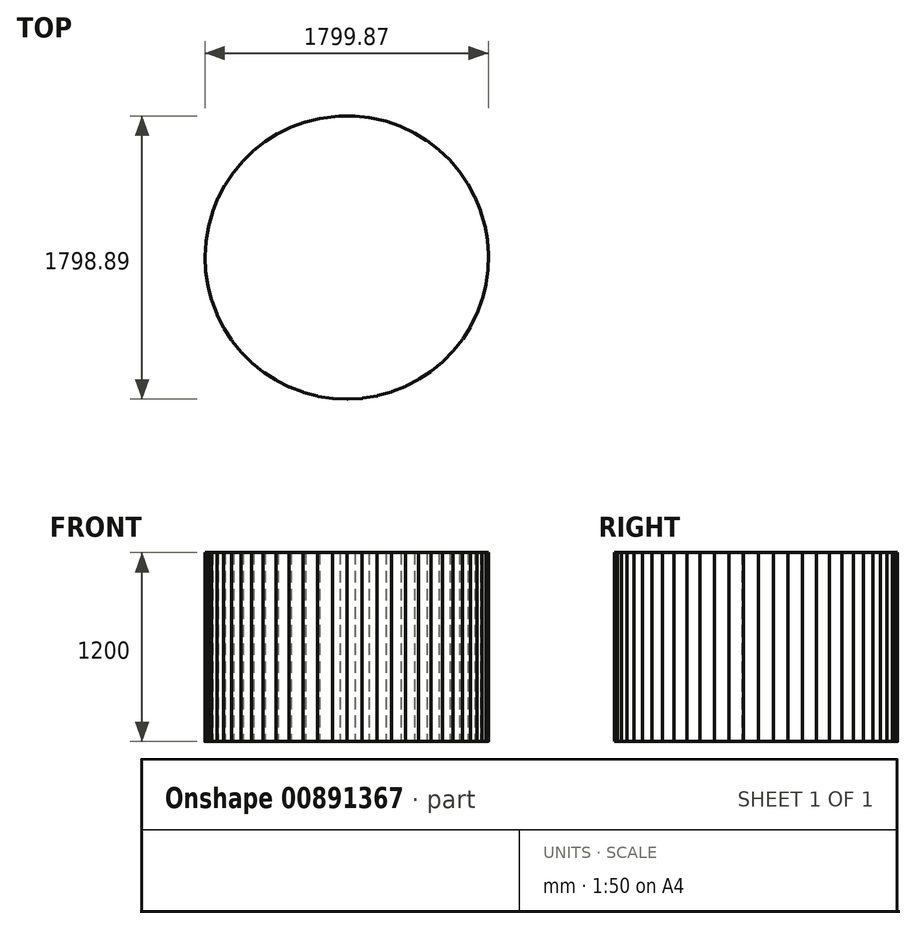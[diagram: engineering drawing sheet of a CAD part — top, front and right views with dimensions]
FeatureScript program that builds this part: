
annotation { "Feature Type Name" : "Feature", "Feature Type Description" : "" }
export const myFeature = defineFeature(function(context is Context, id is Id, definition is map)
    precondition{}
    {
        {
            var Q0;
            Q0=qCreatedBy(makeId("Top.planeOp"),FACE);
            var sketch = newSketch(context, id + "F0", { "sketchPlane" : qUnion([Q0])});
            skLineSegment(sketch, "E0.bottom", {"start": v(-48.1, 898.71) * mm, "end": v(46.9, 898.71) * mm});
            skLineSegment(sketch, "E0.top", {"start": v(-48.1, 853.71) * mm, "end": v(46.9, 853.71) * mm});
            skArc(sketch, "E1", {"start": v(46.9, 853.71) * mm, "mid": v(69.4, 876.21) * mm, "end": v(46.9, 898.71) * mm});
            skLineSegment(sketch, "E2", {"start": v(46.9, 898.71) * mm, "end": v(141.37, 888.83) * mm});
            skLineSegment(sketch, "E3.0", {"start": v(42.2, 853.96) * mm, "end": v(136.69, 844.07) * mm});
            skArc(sketch, "E4", {"start": v(141.37, 888.83) * mm, "mid": v(161.4, 864.1) * mm, "end": v(136.69, 844.07) * mm});
            skLineSegment(sketch, "E5", {"start": v(141.37, 888.83) * mm, "end": v(249.54, 864.71) * mm});
            skLineSegment(sketch, "E6.0", {"start": v(147.03, 841.46) * mm, "end": v(239.75, 820.8) * mm});
            skArc(sketch, "E7", {"start": v(249.54, 864.71) * mm, "mid": v(266.6, 837.86) * mm, "end": v(239.75, 820.8) * mm});
            skLineSegment(sketch, "E8", {"start": v(249.54, 864.71) * mm, "end": v(339.3, 833.6) * mm});
            skLineSegment(sketch, "E9", {"start": v(339.3, 833.6) * mm, "end": v(425.28, 793.18) * mm});
            skLineSegment(sketch, "E10", {"start": v(425.28, 793.18) * mm, "end": v(506.52, 743.94) * mm});
            skLineSegment(sketch, "E11", {"start": v(506.52, 743.94) * mm, "end": v(582.11, 686.4) * mm});
            skLineSegment(sketch, "E12", {"start": v(582.11, 686.4) * mm, "end": v(651.22, 621.22) * mm});
            skLineSegment(sketch, "E13", {"start": v(651.22, 621.22) * mm, "end": v(713.08, 549.11) * mm});
            skLineSegment(sketch, "E14", {"start": v(713.08, 549.11) * mm, "end": v(766.98, 470.89) * mm});
            skLineSegment(sketch, "E15", {"start": v(766.98, 470.89) * mm, "end": v(812.59, 386.91) * mm});
            skLineSegment(sketch, "E16", {"start": v(812.59, 386.91) * mm, "end": v(848.85, 299.1) * mm});
            skLineSegment(sketch, "E17", {"start": v(848.85, 299.1) * mm, "end": v(875.64, 207.96) * mm});
            skLineSegment(sketch, "E18", {"start": v(875.64, 207.96) * mm, "end": v(892.69, 114.5) * mm});
            skLineSegment(sketch, "E19", {"start": v(892.69, 114.5) * mm, "end": v(899.78, 19.77) * mm});
            skLineSegment(sketch, "E20", {"start": v(899.78, 19.77) * mm, "end": v(896.85, -75.19) * mm});
            skLineSegment(sketch, "E21", {"start": v(896.85, -75.19) * mm, "end": v(883.93, -169.3) * mm});
            skLineSegment(sketch, "E22.0", {"start": v(234.8, 822.2) * mm, "end": v(324.56, 791.07) * mm});
            skLineSegment(sketch, "E23.0", {"start": v(320.16, 792.87) * mm, "end": v(406.14, 752.46) * mm});
            skLineSegment(sketch, "E24.0", {"start": v(401.95, 754.7) * mm, "end": v(483.2, 705.45) * mm});
            skLineSegment(sketch, "E25.0", {"start": v(479.26, 708.13) * mm, "end": v(554.86, 650.6) * mm});
            skLineSegment(sketch, "E26.0", {"start": v(551.24, 653.66) * mm, "end": v(620.35, 588.48) * mm});
            skLineSegment(sketch, "E27.0", {"start": v(617.07, 591.92) * mm, "end": v(678.92, 519.81) * mm});
            skLineSegment(sketch, "E28.0", {"start": v(676.02, 523.58) * mm, "end": v(729.93, 445.35) * mm});
            skLineSegment(sketch, "E29.0", {"start": v(727.44, 449.41) * mm, "end": v(773.04, 365.44) * mm});
            skLineSegment(sketch, "E30.0", {"start": v(771, 369.74) * mm, "end": v(807.25, 281.93) * mm});
            skLineSegment(sketch, "E31.0", {"start": v(805.67, 286.4) * mm, "end": v(832.47, 195.27) * mm});
            skLineSegment(sketch, "E32.0", {"start": v(831.37, 199.89) * mm, "end": v(848.42, 106.43) * mm});
            skLineSegment(sketch, "E33.0", {"start": v(847.81, 111.14) * mm, "end": v(854.9, 16.4) * mm});
            skLineSegment(sketch, "E34.0", {"start": v(854.8, 21.15) * mm, "end": v(851.88, -73.8) * mm});
            skLineSegment(sketch, "E35.0", {"start": v(852.27, -69.07) * mm, "end": v(839.35, -163.18) * mm});
            skArc(sketch, "E36", {"start": v(339.3, 833.6) * mm, "mid": v(353.19, 804.96) * mm, "end": v(324.56, 791.07) * mm});
            skArc(sketch, "E37", {"start": v(425.28, 793.18) * mm, "mid": v(436.07, 763.25) * mm, "end": v(406.14, 752.46) * mm});
            skArc(sketch, "E38", {"start": v(506.52, 743.94) * mm, "mid": v(514.1, 713.03) * mm, "end": v(483.2, 705.45) * mm});
            skArc(sketch, "E39", {"start": v(582.11, 686.4) * mm, "mid": v(586.4, 654.87) * mm, "end": v(554.86, 650.6) * mm});
            skArc(sketch, "E40", {"start": v(651.22, 621.22) * mm, "mid": v(652.15, 589.4) * mm, "end": v(620.35, 588.48) * mm});
            skArc(sketch, "E41", {"start": v(713.08, 549.11) * mm, "mid": v(710.65, 517.38) * mm, "end": v(678.92, 519.81) * mm});
            skArc(sketch, "E42", {"start": v(766.98, 470.89) * mm, "mid": v(761.23, 439.6) * mm, "end": v(729.93, 445.35) * mm});
            skArc(sketch, "E43", {"start": v(812.59, 386.91) * mm, "mid": v(803.55, 356.4) * mm, "end": v(773.04, 365.44) * mm});
            skArc(sketch, "E44", {"start": v(848.85, 299.1) * mm, "mid": v(836.64, 269.72) * mm, "end": v(807.25, 281.93) * mm});
            skArc(sketch, "E45", {"start": v(875.64, 207.96) * mm, "mid": v(860.4, 180.03) * mm, "end": v(832.47, 195.27) * mm});
            skArc(sketch, "E46", {"start": v(892.69, 114.5) * mm, "mid": v(874.59, 88.33) * mm, "end": v(848.42, 106.43) * mm});
            skArc(sketch, "E47", {"start": v(899.78, 19.77) * mm, "mid": v(879.03, -4.35) * mm, "end": v(854.9, 16.4) * mm});
            skArc(sketch, "E48", {"start": v(896.85, -75.19) * mm, "mid": v(873.67, -96.98) * mm, "end": v(851.88, -73.8) * mm});
            skArc(sketch, "E49", {"start": v(839.35, -163.18) * mm, "mid": v(858.58, -188.54) * mm, "end": v(883.93, -169.3) * mm});
            skLineSegment(sketch, "E50", {"start": v(883.93, -169.3) * mm, "end": v(861.16, -261.54) * mm});
            skLineSegment(sketch, "E51", {"start": v(861.16, -261.54) * mm, "end": v(828.8, -350.85) * mm});
            skLineSegment(sketch, "E52", {"start": v(828.8, -350.85) * mm, "end": v(787.2, -436.26) * mm});
            skLineSegment(sketch, "E53", {"start": v(787.2, -436.26) * mm, "end": v(736.82, -516.8) * mm});
            skLineSegment(sketch, "E54", {"start": v(736.82, -516.8) * mm, "end": v(678.24, -591.6) * mm});
            skLineSegment(sketch, "E55", {"start": v(678.24, -591.6) * mm, "end": v(612.1, -659.8) * mm});
            skLineSegment(sketch, "E56", {"start": v(612.1, -659.8) * mm, "end": v(539.15, -720.64) * mm});
            skLineSegment(sketch, "E57", {"start": v(539.15, -720.64) * mm, "end": v(460.18, -773.45) * mm});
            skLineSegment(sketch, "E58", {"start": v(460.18, -773.45) * mm, "end": v(376.1, -817.65) * mm});
            skLineSegment(sketch, "E59", {"start": v(376.1, -817.65) * mm, "end": v(287.8, -852.74) * mm});
            skLineSegment(sketch, "E60", {"start": v(287.8, -852.74) * mm, "end": v(196.32, -878.33) * mm});
            skLineSegment(sketch, "E61", {"start": v(196.32, -878.33) * mm, "end": v(102.64, -894.13) * mm});
            skLineSegment(sketch, "E62", {"start": v(102.64, -894.13) * mm, "end": v(7.82, -899.97) * mm});
            skLineSegment(sketch, "E63", {"start": v(7.82, -899.97) * mm, "end": v(-87.09, -895.78) * mm});
            skLineSegment(sketch, "E64", {"start": v(-87.09, -895.78) * mm, "end": v(-181.02, -881.6) * mm});
            skLineSegment(sketch, "E65", {"start": v(-181.02, -881.6) * mm, "end": v(-272.94, -857.61) * mm});
            skLineSegment(sketch, "E66", {"start": v(-272.94, -857.61) * mm, "end": v(-361.82, -824.07) * mm});
            skLineSegment(sketch, "E67", {"start": v(-361.82, -824.07) * mm, "end": v(-446.67, -781.34) * mm});
            skLineSegment(sketch, "E68", {"start": v(-446.67, -781.34) * mm, "end": v(-526.54, -729.9) * mm});
            skLineSegment(sketch, "E69", {"start": v(-526.54, -729.9) * mm, "end": v(-600.55, -670.33) * mm});
            skLineSegment(sketch, "E70", {"start": v(-600.55, -670.33) * mm, "end": v(-667.86, -603.3) * mm});
            skLineSegment(sketch, "E71", {"start": v(-667.86, -603.3) * mm, "end": v(-727.73, -529.54) * mm});
            skLineSegment(sketch, "E72", {"start": v(-727.73, -529.54) * mm, "end": v(-779.5, -449.88) * mm});
            skLineSegment(sketch, "E73", {"start": v(-779.5, -449.88) * mm, "end": v(-822.57, -365.2) * mm});
            skLineSegment(sketch, "E74", {"start": v(-822.57, -365.2) * mm, "end": v(-856.49, -276.47) * mm});
            skLineSegment(sketch, "E75", {"start": v(-856.49, -276.47) * mm, "end": v(-880.86, -184.64) * mm});
            skLineSegment(sketch, "E76", {"start": v(-880.86, -184.64) * mm, "end": v(-895.41, -90.77) * mm});
            skLineSegment(sketch, "E77", {"start": v(-895.41, -90.77) * mm, "end": v(-900, 4.12) * mm});
            skLineSegment(sketch, "E78", {"start": v(-900, 4.12) * mm, "end": v(-894.54, 98.97) * mm});
            skLineSegment(sketch, "E79", {"start": v(-894.54, 98.97) * mm, "end": v(-879.13, 192.7) * mm});
            skLineSegment(sketch, "E80", {"start": v(-879.13, 192.7) * mm, "end": v(-853.92, 284.3) * mm});
            skLineSegment(sketch, "E81", {"start": v(-853.92, 284.3) * mm, "end": v(-819.2, 372.73) * mm});
            skLineSegment(sketch, "E82", {"start": v(-819.2, 372.73) * mm, "end": v(-775.34, 457) * mm});
            skLineSegment(sketch, "E83", {"start": v(-775.34, 457) * mm, "end": v(-722.85, 536.18) * mm});
            skLineSegment(sketch, "E84", {"start": v(-722.85, 536.18) * mm, "end": v(-662.3, 609.39) * mm});
            skLineSegment(sketch, "E85", {"start": v(-662.3, 609.39) * mm, "end": v(-594.38, 675.8) * mm});
            skLineSegment(sketch, "E86.0", {"start": v(840.24, -158.52) * mm, "end": v(817.47, -250.75) * mm});
            skLineSegment(sketch, "E87.0", {"start": v(818.85, -246.2) * mm, "end": v(786.49, -335.52) * mm});
            skLineSegment(sketch, "E88.0", {"start": v(788.34, -331.15) * mm, "end": v(746.74, -416.55) * mm});
            skLineSegment(sketch, "E89.0", {"start": v(749.04, -412.4) * mm, "end": v(698.67, -492.95) * mm});
            skLineSegment(sketch, "E90.0", {"start": v(701.4, -489.06) * mm, "end": v(642.82, -563.85) * mm});
            skLineSegment(sketch, "E91.0", {"start": v(645.94, -560.27) * mm, "end": v(579.8, -628.46) * mm});
            skLineSegment(sketch, "E92.0", {"start": v(583.29, -625.23) * mm, "end": v(510.33, -686.08) * mm});
            skLineSegment(sketch, "E93.0", {"start": v(514.13, -683.23) * mm, "end": v(435.17, -736.05) * mm});
            skLineSegment(sketch, "E94.0", {"start": v(439.25, -733.62) * mm, "end": v(355.16, -777.82) * mm});
            skLineSegment(sketch, "E95.0", {"start": v(359.47, -775.83) * mm, "end": v(271.19, -810.92) * mm});
            skLineSegment(sketch, "E96.0", {"start": v(275.69, -809.4) * mm, "end": v(184.2, -835) * mm});
            skLineSegment(sketch, "E97.0", {"start": v(188.84, -833.95) * mm, "end": v(95.16, -849.75) * mm});
            skLineSegment(sketch, "E98.0", {"start": v(99.88, -849.21) * mm, "end": v(5.06, -855.05) * mm});
            skLineSegment(sketch, "E99.0", {"start": v(9.8, -855) * mm, "end": v(-85.1, -850.82) * mm});
            skLineSegment(sketch, "E100.0", {"start": v(-80.37, -851.28) * mm, "end": v(-174.31, -837.11) * mm});
            skLineSegment(sketch, "E101.0", {"start": v(-169.66, -838.07) * mm, "end": v(-261.58, -814.07) * mm});
            skLineSegment(sketch, "E102.0", {"start": v(-257.05, -815.51) * mm, "end": v(-345.93, -781.97) * mm});
            skLineSegment(sketch, "E103.0", {"start": v(-341.58, -783.88) * mm, "end": v(-426.43, -741.15) * mm});
            skLineSegment(sketch, "E104.0", {"start": v(-422.3, -743.5) * mm, "end": v(-502.18, -692.07) * mm});
            skLineSegment(sketch, "E105.0", {"start": v(-498.32, -694.85) * mm, "end": v(-572.33, -635.28) * mm});
            skLineSegment(sketch, "E106.0", {"start": v(-568.8, -638.45) * mm, "end": v(-636.1, -571.41) * mm});
            skLineSegment(sketch, "E107.0", {"start": v(-632.92, -574.94) * mm, "end": v(-692.8, -501.18) * mm});
            skLineSegment(sketch, "E108.0", {"start": v(-690, -505.02) * mm, "end": v(-741.76, -425.36) * mm});
            skLineSegment(sketch, "E109.0", {"start": v(-739.39, -429.47) * mm, "end": v(-782.46, -344.8) * mm});
            skLineSegment(sketch, "E110.0", {"start": v(-780.54, -349.14) * mm, "end": v(-814.45, -260.4) * mm});
            skLineSegment(sketch, "E111.0", {"start": v(-813, -264.92) * mm, "end": v(-837.36, -173.1) * mm});
            skLineSegment(sketch, "E112.0", {"start": v(-836.39, -177.75) * mm, "end": v(-850.94, -83.87) * mm});
            skLineSegment(sketch, "E113.0", {"start": v(-850.46, -88.6) * mm, "end": v(-855.04, 6.3) * mm});
            skLineSegment(sketch, "E114.0", {"start": v(-855.06, 1.54) * mm, "end": v(-849.62, 96.39) * mm});
            skLineSegment(sketch, "E115.0", {"start": v(-850.14, 91.66) * mm, "end": v(-834.72, 185.4) * mm});
            skLineSegment(sketch, "E116.0", {"start": v(-835.74, 180.77) * mm, "end": v(-810.53, 272.36) * mm});
            skLineSegment(sketch, "E117.0", {"start": v(-812.03, 267.85) * mm, "end": v(-777.3, 356.28) * mm});
            skLineSegment(sketch, "E118.0", {"start": v(-779.27, 351.96) * mm, "end": v(-735.42, 436.23) * mm});
            skLineSegment(sketch, "E119.0", {"start": v(-737.83, 432.14) * mm, "end": v(-685.34, 511.32) * mm});
            skLineSegment(sketch, "E120.0", {"start": v(-688.17, 507.5) * mm, "end": v(-627.63, 580.7) * mm});
            skLineSegment(sketch, "E121.0", {"start": v(-630.84, 577.21) * mm, "end": v(-562.92, 643.63) * mm});
            skArc(sketch, "E122", {"start": v(817.47, -250.75) * mm, "mid": v(833.92, -277.99) * mm, "end": v(861.16, -261.54) * mm});
            skArc(sketch, "E123", {"start": v(828.8, -350.85) * mm, "mid": v(799.98, -364.34) * mm, "end": v(786.49, -335.52) * mm});
            skArc(sketch, "E124", {"start": v(787.2, -436.26) * mm, "mid": v(757.12, -446.64) * mm, "end": v(746.74, -416.55) * mm});
            skArc(sketch, "E125", {"start": v(736.82, -516.8) * mm, "mid": v(705.82, -523.95) * mm, "end": v(698.67, -492.95) * mm});
            skArc(sketch, "E126", {"start": v(678.24, -591.6) * mm, "mid": v(646.66, -595.43) * mm, "end": v(642.82, -563.85) * mm});
            skArc(sketch, "E127", {"start": v(612.1, -659.8) * mm, "mid": v(580.3, -660.28) * mm, "end": v(579.8, -628.46) * mm});
            skArc(sketch, "E128", {"start": v(539.15, -720.64) * mm, "mid": v(507.46, -717.77) * mm, "end": v(510.33, -686.08) * mm});
            skArc(sketch, "E129", {"start": v(460.18, -773.45) * mm, "mid": v(428.97, -767.26) * mm, "end": v(435.17, -736.05) * mm});
            skArc(sketch, "E130", {"start": v(376.1, -817.65) * mm, "mid": v(345.7, -808.2) * mm, "end": v(355.16, -777.82) * mm});
            skArc(sketch, "E131", {"start": v(287.8, -852.74) * mm, "mid": v(258.59, -840.14) * mm, "end": v(271.19, -810.92) * mm});
            skArc(sketch, "E132", {"start": v(196.32, -878.33) * mm, "mid": v(168.6, -862.72) * mm, "end": v(184.2, -835) * mm});
            skArc(sketch, "E133", {"start": v(102.64, -894.13) * mm, "mid": v(76.71, -875.68) * mm, "end": v(95.16, -849.75) * mm});
            skArc(sketch, "E134", {"start": v(7.82, -899.97) * mm, "mid": v(-16.02, -878.9) * mm, "end": v(5.06, -855.05) * mm});
            skArc(sketch, "E135", {"start": v(-87.09, -895.78) * mm, "mid": v(-108.57, -872.3) * mm, "end": v(-85.1, -850.82) * mm});
            skArc(sketch, "E136", {"start": v(-181.02, -881.6) * mm, "mid": v(-199.91, -856) * mm, "end": v(-174.31, -837.11) * mm});
            skArc(sketch, "E137", {"start": v(-272.94, -857.61) * mm, "mid": v(-288.4, -827.73) * mm, "end": v(-257.05, -815.51) * mm});
            skArc(sketch, "E138", {"start": v(-361.82, -824.07) * mm, "mid": v(-374.93, -795.07) * mm, "end": v(-345.93, -781.97) * mm});
            skArc(sketch, "E139", {"start": v(-446.67, -781.34) * mm, "mid": v(-455.52, -748.88) * mm, "end": v(-422.3, -743.5) * mm});
            skArc(sketch, "E140", {"start": v(-526.54, -729.9) * mm, "mid": v(-534.4, -699.23) * mm, "end": v(-504.4, -689.1) * mm});
            skArc(sketch, "E141", {"start": v(-600.55, -670.33) * mm, "mid": v(-603.96, -638.7) * mm, "end": v(-572.33, -635.28) * mm});
            skArc(sketch, "E142", {"start": v(-667.86, -603.3) * mm, "mid": v(-667.92, -571.48) * mm, "end": v(-636.1, -571.41) * mm});
            skArc(sketch, "E143", {"start": v(-727.73, -529.54) * mm, "mid": v(-724.44, -497.89) * mm, "end": v(-692.8, -501.18) * mm});
            skArc(sketch, "E144", {"start": v(-779.5, -449.88) * mm, "mid": v(-772.89, -418.75) * mm, "end": v(-741.76, -425.36) * mm});
            skArc(sketch, "E145", {"start": v(-822.57, -365.2) * mm, "mid": v(-812.72, -334.95) * mm, "end": v(-782.46, -344.8) * mm});
            skArc(sketch, "E146", {"start": v(-856.49, -276.47) * mm, "mid": v(-843.5, -247.42) * mm, "end": v(-814.45, -260.4) * mm});
            skArc(sketch, "E147", {"start": v(-880.86, -184.64) * mm, "mid": v(-864.88, -157.13) * mm, "end": v(-837.36, -173.1) * mm});
            skArc(sketch, "E148", {"start": v(-900, 4.12) * mm, "mid": v(-878.6, 27.68) * mm, "end": v(-855.04, 6.3) * mm});
            skArc(sketch, "E149", {"start": v(-894.54, 98.97) * mm, "mid": v(-870.79, 120.14) * mm, "end": v(-849.62, 96.39) * mm});
            skArc(sketch, "E150", {"start": v(-879.13, 192.7) * mm, "mid": v(-853.27, 211.26) * mm, "end": v(-834.72, 185.4) * mm});
            skArc(sketch, "E151", {"start": v(-853.92, 284.3) * mm, "mid": v(-828.08, 299.93) * mm, "end": v(-811.07, 274.99) * mm});
            skArc(sketch, "E152", {"start": v(-819.2, 372.73) * mm, "mid": v(-790.02, 385.45) * mm, "end": v(-777.3, 356.28) * mm});
            skArc(sketch, "E153", {"start": v(-775.34, 457) * mm, "mid": v(-745, 466.57) * mm, "end": v(-735.42, 436.23) * mm});
            skArc(sketch, "E154", {"start": v(-722.85, 536.18) * mm, "mid": v(-691.3, 543) * mm, "end": v(-683.69, 511.63) * mm});
            skArc(sketch, "E155", {"start": v(-662.3, 609.39) * mm, "mid": v(-630.58, 612.2) * mm, "end": v(-628.15, 580.45) * mm});
            skLineSegment(sketch, "E156", {"start": v(-594.38, 675.8) * mm, "end": v(-519.83, 734.7) * mm});
            skLineSegment(sketch, "E157", {"start": v(-519.83, 734.7) * mm, "end": v(-439.5, 785.4) * mm});
            skLineSegment(sketch, "E158", {"start": v(-439.5, 785.4) * mm, "end": v(-354.26, 827.35) * mm});
            skLineSegment(sketch, "E159", {"start": v(-354.26, 827.35) * mm, "end": v(-265.07, 860.08) * mm});
            skLineSegment(sketch, "E160", {"start": v(-265.07, 860.08) * mm, "end": v(-172.94, 883.23) * mm});
            skLineSegment(sketch, "E161.0", {"start": v(-566.48, 640.5) * mm, "end": v(-491.94, 699.38) * mm});
            skLineSegment(sketch, "E162.0", {"start": v(-495.81, 696.64) * mm, "end": v(-415.48, 747.34) * mm});
            skLineSegment(sketch, "E163.0", {"start": v(-419.62, 745.02) * mm, "end": v(-334.39, 786.97) * mm});
            skLineSegment(sketch, "E164.0", {"start": v(-338.75, 785.1) * mm, "end": v(-249.57, 817.83) * mm});
            skLineSegment(sketch, "E165.0", {"start": v(-254.1, 816.44) * mm, "end": v(-161.97, 839.59) * mm});
            skLineSegment(sketch, "E166.0", {"start": v(-167.53, 838.83) * mm, "end": v(-42.67, 854.04) * mm});
            skArc(sketch, "E167", {"start": v(-594.38, 675.8) * mm, "mid": v(-562.56, 675.45) * mm, "end": v(-562.92, 643.63) * mm});
            skArc(sketch, "E168", {"start": v(-491.94, 699.38) * mm, "mid": v(-488.1, 731.63) * mm, "end": v(-520.34, 735.57) * mm});
            skArc(sketch, "E169", {"start": v(-415.48, 747.34) * mm, "mid": v(-408.46, 778.38) * mm, "end": v(-439.5, 785.4) * mm});
            skArc(sketch, "E170", {"start": v(-334.39, 786.97) * mm, "mid": v(-324.09, 816.72) * mm, "end": v(-353.72, 827.33) * mm});
            skArc(sketch, "E171", {"start": v(-249.57, 817.83) * mm, "mid": v(-236.2, 846.7) * mm, "end": v(-265.07, 860.08) * mm});
            skArc(sketch, "E172", {"start": v(-42.67, 854.04) * mm, "mid": v(-23.05, 879.1) * mm, "end": v(-48.1, 898.71) * mm});
            skArc(sketch, "E173", {"start": v(-172.94, 883.23) * mm, "mid": v(-145.07, 864.1) * mm, "end": v(-167.53, 838.83) * mm});
            skLineSegment(sketch, "E174", {"start": v(-172.94, 883.23) * mm, "end": v(-48.1, 898.71) * mm});
            skSolve(sketch);
        }
        {
            var Q0;
            {var subQ63=sQuery(id+"F0.wireOp",EDGE,"E3.0");var subQ64=sQuery(id+"F0.wireOp",EDGE,"E0.top");var subQ65=makeQuery(id+"F0.imprint","INTERSECT",VERTEX,{"derivedFrom":[subQ64,subQ63]});Q0=makeQuery(id+"F0.imprint","IMPRINT",FACE,{"disambiguationData":[TD([[makeQuery(id+"F0.imprint","IMPRINT",EDGE,{"disambiguationData":[TD([[subQ65,1.0]])],"derivedFrom":subQ64}),-1.0]])]});}
            var Q1;
            {var subQ0=sQuery(id+"F0.wireOp",EDGE,"E126");var subQ1=sQuery(id+"F0.wireOp",EDGE,"E90.0");var subQ2=makeQuery(id+"F0.imprint","INTERSECT",VERTEX,{"derivedFrom":[subQ1,subQ0]});Q1=makeQuery(id+"F0.imprint","IMPRINT",FACE,{"disambiguationData":[TD([[makeQuery(id+"F0.imprint","IMPRINT",EDGE,{"disambiguationData":[TD([[subQ2,1.0]])],"derivedFrom":subQ1}),-1.0]])]});}
            var Q2;
            {var subQ1=sQuery(id+"F0.wireOp",EDGE,"E110.0");var subQ4=sQuery(id+"F0.wireOp",EDGE,"E146");var subQ5=makeQuery(id+"F0.imprint","INTERSECT",VERTEX,{"derivedFrom":[subQ1,subQ4]});Q2=makeQuery(id+"F0.imprint","IMPRINT",FACE,{"disambiguationData":[TD([[makeQuery(id+"F0.imprint","IMPRINT",EDGE,{"disambiguationData":[TD([[subQ5,1.0]])],"derivedFrom":subQ1}),-1.0]])]});}
            var Q3;
            {var subQ1=sQuery(id+"F0.wireOp",EDGE,"E164.0");var subQ5=sQuery(id+"F0.wireOp",EDGE,"E171");var subQ6=makeQuery(id+"F0.imprint","INTERSECT",VERTEX,{"derivedFrom":[subQ1,subQ5]});Q3=makeQuery(id+"F0.imprint","IMPRINT",FACE,{"disambiguationData":[TD([[makeQuery(id+"F0.imprint","IMPRINT",EDGE,{"disambiguationData":[TD([[subQ6,1.0]])],"derivedFrom":subQ1}),-1.0]])]});}
            var Q4;
            {var subQ7=sQuery(id+"F0.wireOp",EDGE,"E150");var subQ8=sQuery(id+"F0.wireOp",EDGE,"E115.0");var subQ9=makeQuery(id+"F0.imprint","INTERSECT",VERTEX,{"derivedFrom":[subQ8,subQ7]});Q4=makeQuery(id+"F0.imprint","IMPRINT",FACE,{"disambiguationData":[TD([[makeQuery(id+"F0.imprint","IMPRINT",EDGE,{"disambiguationData":[TD([[subQ9,1.0]])],"derivedFrom":subQ8}),-1.0]])]});}
            var Q5;
            {var subQ1=sQuery(id+"F0.wireOp",EDGE,"E161.0");var subQ4=sQuery(id+"F0.wireOp",EDGE,"E168");var subQ5=makeQuery(id+"F0.imprint","INTERSECT",VERTEX,{"derivedFrom":[subQ1,subQ4]});Q5=makeQuery(id+"F0.imprint","IMPRINT",FACE,{"disambiguationData":[TD([[makeQuery(id+"F0.imprint","IMPRINT",EDGE,{"disambiguationData":[TD([[subQ5,1.0]])],"derivedFrom":subQ1}),-1.0]])]});}
            var Q6;
            {var subQ1=sQuery(id+"F0.wireOp",EDGE,"E166.0");var subQ5=makeQuery(id+"F0.imprint","INTERSECT",VERTEX,{"derivedFrom":[sQuery(id+"F0.wireOp",EDGE,"E0.top"),subQ1]});Q6=makeQuery(id+"F0.imprint","IMPRINT",FACE,{"disambiguationData":[TD([[makeQuery(id+"F0.imprint","IMPRINT",EDGE,{"disambiguationData":[TD([[subQ5,1.0]])],"derivedFrom":subQ1}),1.0]])]});}
            var Q7;
            {var subQ7=sQuery(id+"F0.wireOp",EDGE,"E159");Q7=makeQuery(id+"F0.imprint","IMPRINT",FACE,{"disambiguationData":[TD([[makeQuery(id+"F0.imprint","IMPRINT",EDGE,{"derivedFrom":subQ7}),-1.0]])]});}
            var Q8;
            {var subQ1=sQuery(id+"F0.wireOp",EDGE,"E106.0");var subQ4=sQuery(id+"F0.wireOp",EDGE,"E142");var subQ5=makeQuery(id+"F0.imprint","INTERSECT",VERTEX,{"derivedFrom":[subQ1,subQ4]});Q8=makeQuery(id+"F0.imprint","IMPRINT",FACE,{"disambiguationData":[TD([[makeQuery(id+"F0.imprint","IMPRINT",EDGE,{"disambiguationData":[TD([[subQ5,1.0]])],"derivedFrom":subQ1}),-1.0]])]});}
            var Q9;
            {var subQ7=sQuery(id+"F0.wireOp",EDGE,"E167");var subQ9=sQuery(id+"F0.wireOp",EDGE,"E121.0");var subQ10=makeQuery(id+"F0.imprint","INTERSECT",VERTEX,{"derivedFrom":[subQ9,subQ7]});Q9=makeQuery(id+"F0.imprint","IMPRINT",FACE,{"disambiguationData":[TD([[makeQuery(id+"F0.imprint","IMPRINT",EDGE,{"disambiguationData":[TD([[subQ10,1.0]])],"derivedFrom":subQ9}),-1.0]])]});}
            var Q10;
            {var subQ1=sQuery(id+"F0.wireOp",EDGE,"E24.0");var subQ4=sQuery(id+"F0.wireOp",EDGE,"E38");var subQ5=makeQuery(id+"F0.imprint","INTERSECT",VERTEX,{"derivedFrom":[subQ1,subQ4]});Q10=makeQuery(id+"F0.imprint","IMPRINT",FACE,{"disambiguationData":[TD([[makeQuery(id+"F0.imprint","IMPRINT",EDGE,{"disambiguationData":[TD([[subQ5,1.0]])],"derivedFrom":subQ1}),-1.0]])]});}
            var Q11;
            {var subQ0=sQuery(id+"F0.wireOp",EDGE,"E174");var subQ1=sQuery(id+"F0.wireOp",EDGE,"E173");var subQ3=makeQuery(id+"F0.imprint","INTERSECT",VERTEX,{"derivedFrom":[subQ1,subQ0]});Q11=makeQuery(id+"F0.imprint","IMPRINT",FACE,{"disambiguationData":[TD([[makeQuery(id+"F0.imprint","IMPRINT",EDGE,{"disambiguationData":[TD([[subQ3,1.0]])],"derivedFrom":subQ1}),-1.0]])]});}
            var Q12;
            {var subQ0=sQuery(id+"F0.wireOp",EDGE,"E125");var subQ1=sQuery(id+"F0.wireOp",EDGE,"E89.0");var subQ2=makeQuery(id+"F0.imprint","INTERSECT",VERTEX,{"derivedFrom":[subQ1,subQ0]});Q12=makeQuery(id+"F0.imprint","IMPRINT",FACE,{"disambiguationData":[TD([[makeQuery(id+"F0.imprint","IMPRINT",EDGE,{"disambiguationData":[TD([[subQ2,1.0]])],"derivedFrom":subQ1}),-1.0]])]});}
            var Q13;
            {var subQ0=sQuery(id+"F0.wireOp",EDGE,"E129");var subQ1=sQuery(id+"F0.wireOp",EDGE,"E93.0");var subQ2=makeQuery(id+"F0.imprint","INTERSECT",VERTEX,{"derivedFrom":[subQ1,subQ0]});Q13=makeQuery(id+"F0.imprint","IMPRINT",FACE,{"disambiguationData":[TD([[makeQuery(id+"F0.imprint","IMPRINT",EDGE,{"disambiguationData":[TD([[subQ2,1.0]])],"derivedFrom":subQ1}),-1.0]])]});}
            var Q14;
            {var subQ0=sQuery(id+"F0.wireOp",EDGE,"E38");var subQ1=sQuery(id+"F0.wireOp",EDGE,"E11");var subQ3=makeQuery(id+"F0.imprint","INTERSECT",VERTEX,{"derivedFrom":[subQ1,subQ0]});Q14=makeQuery(id+"F0.imprint","IMPRINT",FACE,{"disambiguationData":[TD([[makeQuery(id+"F0.imprint","IMPRINT",EDGE,{"disambiguationData":[TD([[subQ3,1.0]])],"derivedFrom":subQ1}),1.0]])]});}
            var Q15;
            {var subQ3=sQuery(id+"F0.wireOp",EDGE,"E118.0");var subQ5=sQuery(id+"F0.wireOp",EDGE,"E153");var subQ6=makeQuery(id+"F0.imprint","INTERSECT",VERTEX,{"derivedFrom":[subQ3,subQ5]});Q15=makeQuery(id+"F0.imprint","IMPRINT",FACE,{"disambiguationData":[TD([[makeQuery(id+"F0.imprint","IMPRINT",EDGE,{"disambiguationData":[TD([[subQ6,1.0]])],"derivedFrom":subQ3}),-1.0]])]});}
            var Q16;
            {var subQ0=sQuery(id+"F0.wireOp",EDGE,"E154");var subQ1=sQuery(id+"F0.wireOp",EDGE,"E84");var subQ3=makeQuery(id+"F0.imprint","INTERSECT",VERTEX,{"derivedFrom":[subQ1,subQ0]});Q16=makeQuery(id+"F0.imprint","IMPRINT",FACE,{"disambiguationData":[TD([[makeQuery(id+"F0.imprint","IMPRINT",EDGE,{"disambiguationData":[TD([[subQ3,1.0]])],"derivedFrom":subQ1}),1.0]])]});}
            var Q17;
            {var subQ0=sQuery(id+"F0.wireOp",EDGE,"E123");var subQ1=sQuery(id+"F0.wireOp",EDGE,"E87.0");var subQ2=makeQuery(id+"F0.imprint","INTERSECT",VERTEX,{"derivedFrom":[subQ1,subQ0]});Q17=makeQuery(id+"F0.imprint","IMPRINT",FACE,{"disambiguationData":[TD([[makeQuery(id+"F0.imprint","IMPRINT",EDGE,{"disambiguationData":[TD([[subQ2,1.0]])],"derivedFrom":subQ1}),-1.0]])]});}
            var Q18;
            {var subQ1=sQuery(id+"F0.wireOp",EDGE,"E108.0");var subQ4=sQuery(id+"F0.wireOp",EDGE,"E144");var subQ5=makeQuery(id+"F0.imprint","INTERSECT",VERTEX,{"derivedFrom":[subQ1,subQ4]});Q18=makeQuery(id+"F0.imprint","IMPRINT",FACE,{"disambiguationData":[TD([[makeQuery(id+"F0.imprint","IMPRINT",EDGE,{"disambiguationData":[TD([[subQ5,1.0]])],"derivedFrom":subQ1}),-1.0]])]});}
            var Q19;
            {var subQ0=sQuery(id+"F0.wireOp",EDGE,"E39");var subQ1=sQuery(id+"F0.wireOp",EDGE,"E12");var subQ3=makeQuery(id+"F0.imprint","INTERSECT",VERTEX,{"derivedFrom":[subQ1,subQ0]});Q19=makeQuery(id+"F0.imprint","IMPRINT",FACE,{"disambiguationData":[TD([[makeQuery(id+"F0.imprint","IMPRINT",EDGE,{"disambiguationData":[TD([[subQ3,1.0]])],"derivedFrom":subQ1}),1.0]])]});}
            var Q20;
            {var subQ1=sQuery(id+"F0.wireOp",EDGE,"E102.0");var subQ5=sQuery(id+"F0.wireOp",EDGE,"E138");var subQ6=makeQuery(id+"F0.imprint","INTERSECT",VERTEX,{"derivedFrom":[subQ1,subQ5]});Q20=makeQuery(id+"F0.imprint","IMPRINT",FACE,{"disambiguationData":[TD([[makeQuery(id+"F0.imprint","IMPRINT",EDGE,{"disambiguationData":[TD([[subQ6,1.0]])],"derivedFrom":subQ1}),-1.0]])]});}
            var Q21;
            {var subQ0=sQuery(id+"F0.wireOp",EDGE,"E130");var subQ1=sQuery(id+"F0.wireOp",EDGE,"E94.0");var subQ2=makeQuery(id+"F0.imprint","INTERSECT",VERTEX,{"derivedFrom":[subQ1,subQ0]});Q21=makeQuery(id+"F0.imprint","IMPRINT",FACE,{"disambiguationData":[TD([[makeQuery(id+"F0.imprint","IMPRINT",EDGE,{"disambiguationData":[TD([[subQ2,1.0]])],"derivedFrom":subQ1}),-1.0]])]});}
            var Q22;
            {var subQ1=sQuery(id+"F0.wireOp",EDGE,"E107.0");var subQ4=sQuery(id+"F0.wireOp",EDGE,"E143");var subQ5=makeQuery(id+"F0.imprint","INTERSECT",VERTEX,{"derivedFrom":[subQ1,subQ4]});Q22=makeQuery(id+"F0.imprint","IMPRINT",FACE,{"disambiguationData":[TD([[makeQuery(id+"F0.imprint","IMPRINT",EDGE,{"disambiguationData":[TD([[subQ5,1.0]])],"derivedFrom":subQ1}),-1.0]])]});}
            var Q23;
            {var subQ1=sQuery(id+"F0.wireOp",EDGE,"E23.0");var subQ4=sQuery(id+"F0.wireOp",EDGE,"E37");var subQ5=makeQuery(id+"F0.imprint","INTERSECT",VERTEX,{"derivedFrom":[subQ1,subQ4]});Q23=makeQuery(id+"F0.imprint","IMPRINT",FACE,{"disambiguationData":[TD([[makeQuery(id+"F0.imprint","IMPRINT",EDGE,{"disambiguationData":[TD([[subQ5,1.0]])],"derivedFrom":subQ1}),-1.0]])]});}
            var Q24;
            {var subQ0=sQuery(id+"F0.wireOp",EDGE,"E166.0");var subQ1=sQuery(id+"F0.wireOp",EDGE,"E165.0");var subQ2=makeQuery(id+"F0.imprint","INTERSECT",VERTEX,{"derivedFrom":[subQ1,subQ0]});Q24=makeQuery(id+"F0.imprint","IMPRINT",FACE,{"disambiguationData":[TD([[makeQuery(id+"F0.imprint","IMPRINT",EDGE,{"disambiguationData":[TD([[subQ2,1.0]])],"derivedFrom":subQ1}),1.0]])]});}
            var Q25;
            {var subQ1=sQuery(id+"F0.wireOp",EDGE,"E25.0");var subQ4=sQuery(id+"F0.wireOp",EDGE,"E39");var subQ5=makeQuery(id+"F0.imprint","INTERSECT",VERTEX,{"derivedFrom":[subQ1,subQ4]});Q25=makeQuery(id+"F0.imprint","IMPRINT",FACE,{"disambiguationData":[TD([[makeQuery(id+"F0.imprint","IMPRINT",EDGE,{"disambiguationData":[TD([[subQ5,1.0]])],"derivedFrom":subQ1}),-1.0]])]});}
            var Q26;
            {var subQ1=sQuery(id+"F0.wireOp",EDGE,"E109.0");var subQ4=sQuery(id+"F0.wireOp",EDGE,"E145");var subQ5=makeQuery(id+"F0.imprint","INTERSECT",VERTEX,{"derivedFrom":[subQ1,subQ4]});Q26=makeQuery(id+"F0.imprint","IMPRINT",FACE,{"disambiguationData":[TD([[makeQuery(id+"F0.imprint","IMPRINT",EDGE,{"disambiguationData":[TD([[subQ5,1.0]])],"derivedFrom":subQ1}),-1.0]])]});}
            var Q27;
            {var subQ0=sQuery(id+"F0.wireOp",EDGE,"E122");var subQ1=sQuery(id+"F0.wireOp",EDGE,"E86.0");var subQ2=makeQuery(id+"F0.imprint","INTERSECT",VERTEX,{"derivedFrom":[subQ1,subQ0]});Q27=makeQuery(id+"F0.imprint","IMPRINT",FACE,{"disambiguationData":[TD([[makeQuery(id+"F0.imprint","IMPRINT",EDGE,{"disambiguationData":[TD([[subQ2,1.0]])],"derivedFrom":subQ1}),-1.0]])]});}
            var Q28;
            {var subQ0=sQuery(id+"F0.wireOp",EDGE,"E121.0");var subQ1=sQuery(id+"F0.wireOp",EDGE,"E120.0");var subQ2=makeQuery(id+"F0.imprint","INTERSECT",VERTEX,{"derivedFrom":[subQ1,subQ0]});Q28=makeQuery(id+"F0.imprint","IMPRINT",FACE,{"disambiguationData":[TD([[makeQuery(id+"F0.imprint","IMPRINT",EDGE,{"disambiguationData":[TD([[subQ2,1.0]])],"derivedFrom":subQ1}),1.0]])]});}
            var Q29;
            {var subQ1=sQuery(id+"F0.wireOp",EDGE,"E117.0");var subQ4=sQuery(id+"F0.wireOp",EDGE,"E152");var subQ5=makeQuery(id+"F0.imprint","INTERSECT",VERTEX,{"derivedFrom":[subQ1,subQ4]});Q29=makeQuery(id+"F0.imprint","IMPRINT",FACE,{"disambiguationData":[TD([[makeQuery(id+"F0.imprint","IMPRINT",EDGE,{"disambiguationData":[TD([[subQ5,1.0]])],"derivedFrom":subQ1}),-1.0]])]});}
            var Q30;
            {var subQ0=sQuery(id+"F0.wireOp",EDGE,"E138");var subQ1=sQuery(id+"F0.wireOp",EDGE,"E67");var subQ3=makeQuery(id+"F0.imprint","INTERSECT",VERTEX,{"derivedFrom":[subQ1,subQ0]});Q30=makeQuery(id+"F0.imprint","IMPRINT",FACE,{"disambiguationData":[TD([[makeQuery(id+"F0.imprint","IMPRINT",EDGE,{"disambiguationData":[TD([[subQ3,1.0]])],"derivedFrom":subQ1}),1.0]])]});}
            var Q31;
            {var subQ0=sQuery(id+"F0.wireOp",EDGE,"E167");var subQ1=sQuery(id+"F0.wireOp",EDGE,"E156");var subQ3=makeQuery(id+"F0.imprint","INTERSECT",VERTEX,{"derivedFrom":[subQ1,subQ0]});Q31=makeQuery(id+"F0.imprint","IMPRINT",FACE,{"disambiguationData":[TD([[makeQuery(id+"F0.imprint","IMPRINT",EDGE,{"disambiguationData":[TD([[subQ3,1.0]])],"derivedFrom":subQ1}),1.0]])]});}
            var Q32;
            {var subQ0=sQuery(id+"F0.wireOp",EDGE,"E146");var subQ1=sQuery(id+"F0.wireOp",EDGE,"E75");var subQ3=makeQuery(id+"F0.imprint","INTERSECT",VERTEX,{"derivedFrom":[subQ1,subQ0]});Q32=makeQuery(id+"F0.imprint","IMPRINT",FACE,{"disambiguationData":[TD([[makeQuery(id+"F0.imprint","IMPRINT",EDGE,{"disambiguationData":[TD([[subQ3,1.0]])],"derivedFrom":subQ1}),1.0]])]});}
            var Q33;
            {var subQ0=sQuery(id+"F0.wireOp",EDGE,"E50");var subQ1=sQuery(id+"F0.wireOp",EDGE,"E49");var subQ3=makeQuery(id+"F0.imprint","INTERSECT",VERTEX,{"derivedFrom":[subQ1,subQ0]});Q33=makeQuery(id+"F0.imprint","IMPRINT",FACE,{"disambiguationData":[TD([[makeQuery(id+"F0.imprint","IMPRINT",EDGE,{"disambiguationData":[TD([[subQ3,-1.0]])],"derivedFrom":subQ1}),1.0]])]});}
            var Q34;
            {var subQ0=sQuery(id+"F0.wireOp",EDGE,"E127");var subQ1=sQuery(id+"F0.wireOp",EDGE,"E56");var subQ3=makeQuery(id+"F0.imprint","INTERSECT",VERTEX,{"derivedFrom":[subQ1,subQ0]});Q34=makeQuery(id+"F0.imprint","IMPRINT",FACE,{"disambiguationData":[TD([[makeQuery(id+"F0.imprint","IMPRINT",EDGE,{"disambiguationData":[TD([[subQ3,1.0]])],"derivedFrom":subQ1}),1.0]])]});}
            var Q35;
            {var subQ1=sQuery(id+"F0.wireOp",EDGE,"E105.0");var subQ4=sQuery(id+"F0.wireOp",EDGE,"E141");var subQ5=makeQuery(id+"F0.imprint","INTERSECT",VERTEX,{"derivedFrom":[subQ1,subQ4]});Q35=makeQuery(id+"F0.imprint","IMPRINT",FACE,{"disambiguationData":[TD([[makeQuery(id+"F0.imprint","IMPRINT",EDGE,{"disambiguationData":[TD([[subQ5,1.0]])],"derivedFrom":subQ1}),-1.0]])]});}
            var Q36;
            {var subQ0=sQuery(id+"F0.wireOp",EDGE,"E155");var subQ1=sQuery(id+"F0.wireOp",EDGE,"E85");var subQ3=makeQuery(id+"F0.imprint","INTERSECT",VERTEX,{"derivedFrom":[subQ1,subQ0]});Q36=makeQuery(id+"F0.imprint","IMPRINT",FACE,{"disambiguationData":[TD([[makeQuery(id+"F0.imprint","IMPRINT",EDGE,{"disambiguationData":[TD([[subQ3,1.0]])],"derivedFrom":subQ1}),1.0]])]});}
            var Q37;
            {var subQ0=sQuery(id+"F0.wireOp",EDGE,"E131");var subQ1=sQuery(id+"F0.wireOp",EDGE,"E60");var subQ3=makeQuery(id+"F0.imprint","INTERSECT",VERTEX,{"derivedFrom":[subQ1,subQ0]});Q37=makeQuery(id+"F0.imprint","IMPRINT",FACE,{"disambiguationData":[TD([[makeQuery(id+"F0.imprint","IMPRINT",EDGE,{"disambiguationData":[TD([[subQ3,1.0]])],"derivedFrom":subQ1}),1.0]])]});}
            var Q38;
            {var subQ0=sQuery(id+"F0.wireOp",EDGE,"E123");var subQ1=sQuery(id+"F0.wireOp",EDGE,"E52");var subQ3=makeQuery(id+"F0.imprint","INTERSECT",VERTEX,{"derivedFrom":[subQ1,subQ0]});Q38=makeQuery(id+"F0.imprint","IMPRINT",FACE,{"disambiguationData":[TD([[makeQuery(id+"F0.imprint","IMPRINT",EDGE,{"disambiguationData":[TD([[subQ3,1.0]])],"derivedFrom":subQ1}),1.0]])]});}
            var Q39;
            {var subQ0=sQuery(id+"F0.wireOp",EDGE,"E169");var subQ1=sQuery(id+"F0.wireOp",EDGE,"E158");var subQ3=makeQuery(id+"F0.imprint","INTERSECT",VERTEX,{"derivedFrom":[subQ1,subQ0]});Q39=makeQuery(id+"F0.imprint","IMPRINT",FACE,{"disambiguationData":[TD([[makeQuery(id+"F0.imprint","IMPRINT",EDGE,{"disambiguationData":[TD([[subQ3,1.0]])],"derivedFrom":subQ1}),1.0]])]});}
            var Q40;
            {var subQ5=sQuery(id+"F0.wireOp",EDGE,"E49");var subQ6=sQuery(id+"F0.wireOp",EDGE,"E35.0");var subQ7=makeQuery(id+"F0.imprint","INTERSECT",VERTEX,{"derivedFrom":[subQ6,subQ5]});Q40=makeQuery(id+"F0.imprint","IMPRINT",FACE,{"disambiguationData":[TD([[makeQuery(id+"F0.imprint","IMPRINT",EDGE,{"disambiguationData":[TD([[subQ7,1.0]])],"derivedFrom":subQ6}),-1.0]])]});}
            var Q41;
            {var subQ1=sQuery(id+"F0.wireOp",EDGE,"E102.0");var subQ3=makeQuery(id+"F0.imprint","INTERSECT",VERTEX,{"derivedFrom":[subQ1,sQuery(id+"F0.wireOp",EDGE,"E103.0")]});Q41=makeQuery(id+"F0.imprint","IMPRINT",FACE,{"disambiguationData":[TD([[makeQuery(id+"F0.imprint","IMPRINT",EDGE,{"disambiguationData":[TD([[subQ3,1.0]])],"derivedFrom":subQ1}),1.0]])]});}
            var Q42;
            {var subQ0=sQuery(id+"F0.wireOp",EDGE,"E124");var subQ1=sQuery(id+"F0.wireOp",EDGE,"E53");var subQ3=makeQuery(id+"F0.imprint","INTERSECT",VERTEX,{"derivedFrom":[subQ1,subQ0]});Q42=makeQuery(id+"F0.imprint","IMPRINT",FACE,{"disambiguationData":[TD([[makeQuery(id+"F0.imprint","IMPRINT",EDGE,{"disambiguationData":[TD([[subQ3,1.0]])],"derivedFrom":subQ1}),1.0]])]});}
            var Q43;
            {var subQ0=sQuery(id+"F0.wireOp",EDGE,"E151");var subQ1=sQuery(id+"F0.wireOp",EDGE,"E81");var subQ3=makeQuery(id+"F0.imprint","INTERSECT",VERTEX,{"derivedFrom":[subQ1,subQ0]});Q43=makeQuery(id+"F0.imprint","IMPRINT",FACE,{"disambiguationData":[TD([[makeQuery(id+"F0.imprint","IMPRINT",EDGE,{"disambiguationData":[TD([[subQ3,1.0]])],"derivedFrom":subQ1}),1.0]])]});}
            var Q44;
            {var subQ0=sQuery(id+"F0.wireOp",EDGE,"E152");var subQ1=sQuery(id+"F0.wireOp",EDGE,"E82");var subQ3=makeQuery(id+"F0.imprint","INTERSECT",VERTEX,{"derivedFrom":[subQ1,subQ0]});Q44=makeQuery(id+"F0.imprint","IMPRINT",FACE,{"disambiguationData":[TD([[makeQuery(id+"F0.imprint","IMPRINT",EDGE,{"disambiguationData":[TD([[subQ3,1.0]])],"derivedFrom":subQ1}),1.0]])]});}
            var Q45;
            {var subQ0=sQuery(id+"F0.wireOp",EDGE,"E127");var subQ1=sQuery(id+"F0.wireOp",EDGE,"E91.0");var subQ2=makeQuery(id+"F0.imprint","INTERSECT",VERTEX,{"derivedFrom":[subQ1,subQ0]});Q45=makeQuery(id+"F0.imprint","IMPRINT",FACE,{"disambiguationData":[TD([[makeQuery(id+"F0.imprint","IMPRINT",EDGE,{"disambiguationData":[TD([[subQ2,1.0]])],"derivedFrom":subQ1}),-1.0]])]});}
            var Q46;
            {var subQ0=sQuery(id+"F0.wireOp",EDGE,"E128");var subQ1=sQuery(id+"F0.wireOp",EDGE,"E92.0");var subQ2=makeQuery(id+"F0.imprint","INTERSECT",VERTEX,{"derivedFrom":[subQ1,subQ0]});Q46=makeQuery(id+"F0.imprint","IMPRINT",FACE,{"disambiguationData":[TD([[makeQuery(id+"F0.imprint","IMPRINT",EDGE,{"disambiguationData":[TD([[subQ2,1.0]])],"derivedFrom":subQ1}),-1.0]])]});}
            var Q47;
            {var subQ0=sQuery(id+"F0.wireOp",EDGE,"E130");var subQ1=sQuery(id+"F0.wireOp",EDGE,"E59");var subQ3=makeQuery(id+"F0.imprint","INTERSECT",VERTEX,{"derivedFrom":[subQ1,subQ0]});Q47=makeQuery(id+"F0.imprint","IMPRINT",FACE,{"disambiguationData":[TD([[makeQuery(id+"F0.imprint","IMPRINT",EDGE,{"disambiguationData":[TD([[subQ3,1.0]])],"derivedFrom":subQ1}),1.0]])]});}
            var Q48;
            {var subQ0=sQuery(id+"F0.wireOp",EDGE,"E171");var subQ1=sQuery(id+"F0.wireOp",EDGE,"E160");var subQ3=makeQuery(id+"F0.imprint","INTERSECT",VERTEX,{"derivedFrom":[subQ1,subQ0]});Q48=makeQuery(id+"F0.imprint","IMPRINT",FACE,{"disambiguationData":[TD([[makeQuery(id+"F0.imprint","IMPRINT",EDGE,{"disambiguationData":[TD([[subQ3,1.0]])],"derivedFrom":subQ1}),1.0]])]});}
            var Q49;
            {var subQ0=sQuery(id+"F0.wireOp",EDGE,"E153");var subQ1=sQuery(id+"F0.wireOp",EDGE,"E83");var subQ3=makeQuery(id+"F0.imprint","INTERSECT",VERTEX,{"derivedFrom":[subQ1,subQ0]});Q49=makeQuery(id+"F0.imprint","IMPRINT",FACE,{"disambiguationData":[TD([[makeQuery(id+"F0.imprint","IMPRINT",EDGE,{"disambiguationData":[TD([[subQ3,1.0]])],"derivedFrom":subQ1}),1.0]])]});}
            var Q50;
            {var subQ0=sQuery(id+"F0.wireOp",EDGE,"E142");var subQ1=sQuery(id+"F0.wireOp",EDGE,"E71");var subQ3=makeQuery(id+"F0.imprint","INTERSECT",VERTEX,{"derivedFrom":[subQ1,subQ0]});Q50=makeQuery(id+"F0.imprint","IMPRINT",FACE,{"disambiguationData":[TD([[makeQuery(id+"F0.imprint","IMPRINT",EDGE,{"disambiguationData":[TD([[subQ3,1.0]])],"derivedFrom":subQ1}),1.0]])]});}
            var Q51;
            {var subQ0=sQuery(id+"F0.wireOp",EDGE,"E166.0");var subQ1=sQuery(id+"F0.wireOp",EDGE,"E165.0");var subQ2=makeQuery(id+"F0.imprint","INTERSECT",VERTEX,{"derivedFrom":[subQ1,subQ0]});Q51=makeQuery(id+"F0.imprint","IMPRINT",FACE,{"disambiguationData":[TD([[makeQuery(id+"F0.imprint","IMPRINT",EDGE,{"disambiguationData":[TD([[subQ2,1.0]])],"derivedFrom":subQ1}),-1.0]])]});}
            var Q52;
            {var subQ1=sQuery(id+"F0.wireOp",EDGE,"E114.0");var subQ4=sQuery(id+"F0.wireOp",EDGE,"E149");var subQ5=makeQuery(id+"F0.imprint","INTERSECT",VERTEX,{"derivedFrom":[subQ1,subQ4]});Q52=makeQuery(id+"F0.imprint","IMPRINT",FACE,{"disambiguationData":[TD([[makeQuery(id+"F0.imprint","IMPRINT",EDGE,{"disambiguationData":[TD([[subQ5,1.0]])],"derivedFrom":subQ1}),-1.0]])]});}
            var Q53;
            {var subQ0=sQuery(id+"F0.wireOp",EDGE,"E140");var subQ1=sQuery(id+"F0.wireOp",EDGE,"E105.0");var subQ2=makeQuery(id+"F0.imprint","INTERSECT",VERTEX,{"derivedFrom":[subQ1,subQ0]});Q53=makeQuery(id+"F0.imprint","IMPRINT",FACE,{"disambiguationData":[TD([[makeQuery(id+"F0.imprint","IMPRINT",EDGE,{"disambiguationData":[TD([[subQ2,-1.0]])],"derivedFrom":subQ1}),1.0]])]});}
            var Q54;
            {var subQ1=sQuery(id+"F0.wireOp",EDGE,"E26.0");var subQ4=sQuery(id+"F0.wireOp",EDGE,"E40");var subQ5=makeQuery(id+"F0.imprint","INTERSECT",VERTEX,{"derivedFrom":[subQ1,subQ4]});Q54=makeQuery(id+"F0.imprint","IMPRINT",FACE,{"disambiguationData":[TD([[makeQuery(id+"F0.imprint","IMPRINT",EDGE,{"disambiguationData":[TD([[subQ5,1.0]])],"derivedFrom":subQ1}),-1.0]])]});}
            var Q55;
            {var subQ0=sQuery(id+"F0.wireOp",EDGE,"E105.0");var subQ1=sQuery(id+"F0.wireOp",EDGE,"E104.0");var subQ2=makeQuery(id+"F0.imprint","INTERSECT",VERTEX,{"derivedFrom":[subQ1,subQ0]});Q55=makeQuery(id+"F0.imprint","IMPRINT",FACE,{"disambiguationData":[TD([[makeQuery(id+"F0.imprint","IMPRINT",EDGE,{"disambiguationData":[TD([[subQ2,1.0]])],"derivedFrom":subQ1}),1.0]])]});}
            var Q56;
            {var subQ1=sQuery(id+"F0.wireOp",EDGE,"E33.0");var subQ4=sQuery(id+"F0.wireOp",EDGE,"E47");var subQ5=makeQuery(id+"F0.imprint","INTERSECT",VERTEX,{"derivedFrom":[subQ1,subQ4]});Q56=makeQuery(id+"F0.imprint","IMPRINT",FACE,{"disambiguationData":[TD([[makeQuery(id+"F0.imprint","IMPRINT",EDGE,{"disambiguationData":[TD([[subQ5,1.0]])],"derivedFrom":subQ1}),-1.0]])]});}
            var Q57;
            {var subQ0=sQuery(id+"F0.wireOp",EDGE,"E40");var subQ1=sQuery(id+"F0.wireOp",EDGE,"E13");var subQ3=makeQuery(id+"F0.imprint","INTERSECT",VERTEX,{"derivedFrom":[subQ1,subQ0]});Q57=makeQuery(id+"F0.imprint","IMPRINT",FACE,{"disambiguationData":[TD([[makeQuery(id+"F0.imprint","IMPRINT",EDGE,{"disambiguationData":[TD([[subQ3,1.0]])],"derivedFrom":subQ1}),1.0]])]});}
            var Q58;
            {var subQ7=sQuery(id+"F0.wireOp",EDGE,"E77");Q58=makeQuery(id+"F0.imprint","IMPRINT",FACE,{"disambiguationData":[TD([[makeQuery(id+"F0.imprint","IMPRINT",EDGE,{"derivedFrom":subQ7}),-1.0]])]});}
            var Q59;
            {var subQ0=sQuery(id+"F0.wireOp",EDGE,"E145");var subQ1=sQuery(id+"F0.wireOp",EDGE,"E74");var subQ3=makeQuery(id+"F0.imprint","INTERSECT",VERTEX,{"derivedFrom":[subQ1,subQ0]});Q59=makeQuery(id+"F0.imprint","IMPRINT",FACE,{"disambiguationData":[TD([[makeQuery(id+"F0.imprint","IMPRINT",EDGE,{"disambiguationData":[TD([[subQ3,1.0]])],"derivedFrom":subQ1}),1.0]])]});}
            var Q60;
            {var subQ0=sQuery(id+"F0.wireOp",EDGE,"E124");var subQ1=sQuery(id+"F0.wireOp",EDGE,"E88.0");var subQ2=makeQuery(id+"F0.imprint","INTERSECT",VERTEX,{"derivedFrom":[subQ1,subQ0]});Q60=makeQuery(id+"F0.imprint","IMPRINT",FACE,{"disambiguationData":[TD([[makeQuery(id+"F0.imprint","IMPRINT",EDGE,{"disambiguationData":[TD([[subQ2,1.0]])],"derivedFrom":subQ1}),-1.0]])]});}
            var Q61;
            {var subQ0=sQuery(id+"F0.wireOp",EDGE,"E126");var subQ1=sQuery(id+"F0.wireOp",EDGE,"E55");var subQ3=makeQuery(id+"F0.imprint","INTERSECT",VERTEX,{"derivedFrom":[subQ1,subQ0]});Q61=makeQuery(id+"F0.imprint","IMPRINT",FACE,{"disambiguationData":[TD([[makeQuery(id+"F0.imprint","IMPRINT",EDGE,{"disambiguationData":[TD([[subQ3,1.0]])],"derivedFrom":subQ1}),1.0]])]});}
            var Q62;
            {var subQ0=sQuery(id+"F0.wireOp",EDGE,"E143");var subQ1=sQuery(id+"F0.wireOp",EDGE,"E72");var subQ3=makeQuery(id+"F0.imprint","INTERSECT",VERTEX,{"derivedFrom":[subQ1,subQ0]});Q62=makeQuery(id+"F0.imprint","IMPRINT",FACE,{"disambiguationData":[TD([[makeQuery(id+"F0.imprint","IMPRINT",EDGE,{"disambiguationData":[TD([[subQ3,1.0]])],"derivedFrom":subQ1}),1.0]])]});}
            var Q63;
            {var subQ0=sQuery(id+"F0.wireOp",EDGE,"E144");var subQ1=sQuery(id+"F0.wireOp",EDGE,"E73");var subQ3=makeQuery(id+"F0.imprint","INTERSECT",VERTEX,{"derivedFrom":[subQ1,subQ0]});Q63=makeQuery(id+"F0.imprint","IMPRINT",FACE,{"disambiguationData":[TD([[makeQuery(id+"F0.imprint","IMPRINT",EDGE,{"disambiguationData":[TD([[subQ3,1.0]])],"derivedFrom":subQ1}),1.0]])]});}
            var Q64;
            {var subQ0=sQuery(id+"F0.wireOp",EDGE,"E37");var subQ1=sQuery(id+"F0.wireOp",EDGE,"E10");var subQ3=makeQuery(id+"F0.imprint","INTERSECT",VERTEX,{"derivedFrom":[subQ1,subQ0]});Q64=makeQuery(id+"F0.imprint","IMPRINT",FACE,{"disambiguationData":[TD([[makeQuery(id+"F0.imprint","IMPRINT",EDGE,{"disambiguationData":[TD([[subQ3,1.0]])],"derivedFrom":subQ1}),1.0]])]});}
            var Q65;
            {var subQ1=sQuery(id+"F0.wireOp",EDGE,"E22.0");var subQ4=sQuery(id+"F0.wireOp",EDGE,"E36");var subQ5=makeQuery(id+"F0.imprint","INTERSECT",VERTEX,{"derivedFrom":[subQ1,subQ4]});Q65=makeQuery(id+"F0.imprint","IMPRINT",FACE,{"disambiguationData":[TD([[makeQuery(id+"F0.imprint","IMPRINT",EDGE,{"disambiguationData":[TD([[subQ5,1.0]])],"derivedFrom":subQ1}),-1.0]])]});}
            var Q66;
            {var subQ0=sQuery(id+"F0.wireOp",EDGE,"E139");var subQ1=sQuery(id+"F0.wireOp",EDGE,"E68");var subQ3=makeQuery(id+"F0.imprint","INTERSECT",VERTEX,{"derivedFrom":[subQ1,subQ0]});Q66=makeQuery(id+"F0.imprint","IMPRINT",FACE,{"disambiguationData":[TD([[makeQuery(id+"F0.imprint","IMPRINT",EDGE,{"disambiguationData":[TD([[subQ3,1.0]])],"derivedFrom":subQ1}),1.0]])]});}
            var Q67;
            {var subQ1=sQuery(id+"F0.wireOp",EDGE,"E32.0");var subQ4=sQuery(id+"F0.wireOp",EDGE,"E46");var subQ5=makeQuery(id+"F0.imprint","INTERSECT",VERTEX,{"derivedFrom":[subQ1,subQ4]});Q67=makeQuery(id+"F0.imprint","IMPRINT",FACE,{"disambiguationData":[TD([[makeQuery(id+"F0.imprint","IMPRINT",EDGE,{"disambiguationData":[TD([[subQ5,1.0]])],"derivedFrom":subQ1}),-1.0]])]});}
            var Q68;
            {var subQ0=sQuery(id+"F0.wireOp",EDGE,"E140");var subQ1=sQuery(id+"F0.wireOp",EDGE,"E69");var subQ3=makeQuery(id+"F0.imprint","INTERSECT",VERTEX,{"derivedFrom":[subQ1,subQ0]});Q68=makeQuery(id+"F0.imprint","IMPRINT",FACE,{"disambiguationData":[TD([[makeQuery(id+"F0.imprint","IMPRINT",EDGE,{"disambiguationData":[TD([[subQ3,1.0]])],"derivedFrom":subQ1}),1.0]])]});}
            var Q69;
            {var subQ0=sQuery(id+"F0.wireOp",EDGE,"E147");var subQ1=sQuery(id+"F0.wireOp",EDGE,"E76");var subQ3=makeQuery(id+"F0.imprint","INTERSECT",VERTEX,{"derivedFrom":[subQ1,subQ0]});Q69=makeQuery(id+"F0.imprint","IMPRINT",FACE,{"disambiguationData":[TD([[makeQuery(id+"F0.imprint","IMPRINT",EDGE,{"disambiguationData":[TD([[subQ3,1.0]])],"derivedFrom":subQ1}),1.0]])]});}
            var Q70;
            {var subQ0=sQuery(id+"F0.wireOp",EDGE,"E48");var subQ1=sQuery(id+"F0.wireOp",EDGE,"E21");var subQ3=makeQuery(id+"F0.imprint","INTERSECT",VERTEX,{"derivedFrom":[subQ1,subQ0]});Q70=makeQuery(id+"F0.imprint","IMPRINT",FACE,{"disambiguationData":[TD([[makeQuery(id+"F0.imprint","IMPRINT",EDGE,{"disambiguationData":[TD([[subQ3,1.0]])],"derivedFrom":subQ1}),1.0]])]});}
            var Q71;
            {var subQ0=sQuery(id+"F0.wireOp",EDGE,"E5");var subQ1=sQuery(id+"F0.wireOp",EDGE,"E4");var subQ3=makeQuery(id+"F0.imprint","INTERSECT",VERTEX,{"derivedFrom":[subQ1,subQ0]});Q71=makeQuery(id+"F0.imprint","IMPRINT",FACE,{"disambiguationData":[TD([[makeQuery(id+"F0.imprint","IMPRINT",EDGE,{"disambiguationData":[TD([[subQ3,1.0]])],"derivedFrom":subQ1}),-1.0]])]});}
            var Q72;
            {var subQ0=sQuery(id+"F0.wireOp",EDGE,"E125");var subQ1=sQuery(id+"F0.wireOp",EDGE,"E54");var subQ3=makeQuery(id+"F0.imprint","INTERSECT",VERTEX,{"derivedFrom":[subQ1,subQ0]});Q72=makeQuery(id+"F0.imprint","IMPRINT",FACE,{"disambiguationData":[TD([[makeQuery(id+"F0.imprint","IMPRINT",EDGE,{"disambiguationData":[TD([[subQ3,1.0]])],"derivedFrom":subQ1}),1.0]])]});}
            var Q73;
            {var subQ0=sQuery(id+"F0.wireOp",EDGE,"E134");var subQ1=sQuery(id+"F0.wireOp",EDGE,"E98.0");var subQ2=makeQuery(id+"F0.imprint","INTERSECT",VERTEX,{"derivedFrom":[subQ1,subQ0]});Q73=makeQuery(id+"F0.imprint","IMPRINT",FACE,{"disambiguationData":[TD([[makeQuery(id+"F0.imprint","IMPRINT",EDGE,{"disambiguationData":[TD([[subQ2,1.0]])],"derivedFrom":subQ1}),-1.0]])]});}
            var Q74;
            {var subQ0=sQuery(id+"F0.wireOp",EDGE,"E129");var subQ1=sQuery(id+"F0.wireOp",EDGE,"E58");var subQ3=makeQuery(id+"F0.imprint","INTERSECT",VERTEX,{"derivedFrom":[subQ1,subQ0]});Q74=makeQuery(id+"F0.imprint","IMPRINT",FACE,{"disambiguationData":[TD([[makeQuery(id+"F0.imprint","IMPRINT",EDGE,{"disambiguationData":[TD([[subQ3,1.0]])],"derivedFrom":subQ1}),1.0]])]});}
            var Q75;
            {var subQ1=sQuery(id+"F0.wireOp",EDGE,"E113.0");var subQ4=sQuery(id+"F0.wireOp",EDGE,"E148");var subQ5=makeQuery(id+"F0.imprint","INTERSECT",VERTEX,{"derivedFrom":[subQ1,subQ4]});Q75=makeQuery(id+"F0.imprint","IMPRINT",FACE,{"disambiguationData":[TD([[makeQuery(id+"F0.imprint","IMPRINT",EDGE,{"disambiguationData":[TD([[subQ5,1.0]])],"derivedFrom":subQ1}),-1.0]])]});}
            var Q76;
            {var subQ0=sQuery(id+"F0.wireOp",EDGE,"E122");var subQ1=sQuery(id+"F0.wireOp",EDGE,"E51");var subQ3=makeQuery(id+"F0.imprint","INTERSECT",VERTEX,{"derivedFrom":[subQ1,subQ0]});Q76=makeQuery(id+"F0.imprint","IMPRINT",FACE,{"disambiguationData":[TD([[makeQuery(id+"F0.imprint","IMPRINT",EDGE,{"disambiguationData":[TD([[subQ3,1.0]])],"derivedFrom":subQ1}),1.0]])]});}
            var Q77;
            {var subQ4=sQuery(id+"F0.wireOp",EDGE,"E1");var subQ6=sQuery(id+"F0.wireOp",EDGE,"E0.top");var subQ7=makeQuery(id+"F0.imprint","INTERSECT",VERTEX,{"derivedFrom":[subQ6,subQ4]});Q77=makeQuery(id+"F0.imprint","IMPRINT",FACE,{"disambiguationData":[TD([[makeQuery(id+"F0.imprint","IMPRINT",EDGE,{"disambiguationData":[TD([[subQ7,1.0]])],"derivedFrom":subQ6}),-1.0]])]});}
            var Q78;
            {var subQ0=sQuery(id+"F0.wireOp",EDGE,"E136");var subQ1=sQuery(id+"F0.wireOp",EDGE,"E100.0");var subQ2=makeQuery(id+"F0.imprint","INTERSECT",VERTEX,{"derivedFrom":[subQ1,subQ0]});Q78=makeQuery(id+"F0.imprint","IMPRINT",FACE,{"disambiguationData":[TD([[makeQuery(id+"F0.imprint","IMPRINT",EDGE,{"disambiguationData":[TD([[subQ2,1.0]])],"derivedFrom":subQ1}),-1.0]])]});}
            var Q79;
            {var subQ0=sQuery(id+"F0.wireOp",EDGE,"E102.0");var subQ1=sQuery(id+"F0.wireOp",EDGE,"E101.0");var subQ2=makeQuery(id+"F0.imprint","INTERSECT",VERTEX,{"derivedFrom":[subQ1,subQ0]});Q79=makeQuery(id+"F0.imprint","IMPRINT",FACE,{"disambiguationData":[TD([[makeQuery(id+"F0.imprint","IMPRINT",EDGE,{"disambiguationData":[TD([[subQ2,1.0]])],"derivedFrom":subQ1}),-1.0]])]});}
            var Q80;
            {var subQ1=sQuery(id+"F0.wireOp",EDGE,"E0.top");var subQ5=makeQuery(id+"F0.imprint","INTERSECT",VERTEX,{"derivedFrom":[subQ1,sQuery(id+"F0.wireOp",EDGE,"E3.0")]});Q80=makeQuery(id+"F0.imprint","IMPRINT",FACE,{"disambiguationData":[TD([[makeQuery(id+"F0.imprint","IMPRINT",EDGE,{"disambiguationData":[TD([[subQ5,1.0]])],"derivedFrom":subQ1}),1.0]])]});}
            var Q81;
            {var subQ0=sQuery(id+"F0.wireOp",EDGE,"E131");var subQ1=sQuery(id+"F0.wireOp",EDGE,"E95.0");var subQ2=makeQuery(id+"F0.imprint","INTERSECT",VERTEX,{"derivedFrom":[subQ1,subQ0]});Q81=makeQuery(id+"F0.imprint","IMPRINT",FACE,{"disambiguationData":[TD([[makeQuery(id+"F0.imprint","IMPRINT",EDGE,{"disambiguationData":[TD([[subQ2,1.0]])],"derivedFrom":subQ1}),-1.0]])]});}
            var Q82;
            {var subQ1=sQuery(id+"F0.wireOp",EDGE,"E31.0");var subQ4=sQuery(id+"F0.wireOp",EDGE,"E45");var subQ5=makeQuery(id+"F0.imprint","INTERSECT",VERTEX,{"derivedFrom":[subQ1,subQ4]});Q82=makeQuery(id+"F0.imprint","IMPRINT",FACE,{"disambiguationData":[TD([[makeQuery(id+"F0.imprint","IMPRINT",EDGE,{"disambiguationData":[TD([[subQ5,1.0]])],"derivedFrom":subQ1}),-1.0]])]});}
            var Q83;
            {var subQ4=sQuery(id+"F0.wireOp",EDGE,"E34.0");var subQ6=sQuery(id+"F0.wireOp",EDGE,"E48");var subQ7=makeQuery(id+"F0.imprint","INTERSECT",VERTEX,{"derivedFrom":[subQ4,subQ6]});Q83=makeQuery(id+"F0.imprint","IMPRINT",FACE,{"disambiguationData":[TD([[makeQuery(id+"F0.imprint","IMPRINT",EDGE,{"disambiguationData":[TD([[subQ7,1.0]])],"derivedFrom":subQ4}),-1.0]])]});}
            var Q84;
            {var subQ0=sQuery(id+"F0.wireOp",EDGE,"E150");var subQ1=sQuery(id+"F0.wireOp",EDGE,"E80");var subQ3=makeQuery(id+"F0.imprint","INTERSECT",VERTEX,{"derivedFrom":[subQ1,subQ0]});Q84=makeQuery(id+"F0.imprint","IMPRINT",FACE,{"disambiguationData":[TD([[makeQuery(id+"F0.imprint","IMPRINT",EDGE,{"disambiguationData":[TD([[subQ3,1.0]])],"derivedFrom":subQ1}),1.0]])]});}
            var Q85;
            {var subQ0=sQuery(id+"F0.wireOp",EDGE,"E172");var subQ1=sQuery(id+"F0.wireOp",EDGE,"E0.bottom");var subQ3=makeQuery(id+"F0.imprint","INTERSECT",VERTEX,{"derivedFrom":[subQ1,subQ0]});Q85=makeQuery(id+"F0.imprint","IMPRINT",FACE,{"disambiguationData":[TD([[makeQuery(id+"F0.imprint","IMPRINT",EDGE,{"disambiguationData":[TD([[subQ3,1.0]])],"derivedFrom":subQ1}),1.0]])]});}
            var Q86;
            {var subQ0=sQuery(id+"F0.wireOp",EDGE,"E149");var subQ1=sQuery(id+"F0.wireOp",EDGE,"E79");var subQ3=makeQuery(id+"F0.imprint","INTERSECT",VERTEX,{"derivedFrom":[subQ1,subQ0]});Q86=makeQuery(id+"F0.imprint","IMPRINT",FACE,{"disambiguationData":[TD([[makeQuery(id+"F0.imprint","IMPRINT",EDGE,{"disambiguationData":[TD([[subQ3,1.0]])],"derivedFrom":subQ1}),1.0]])]});}
            var Q87;
            {var subQ0=sQuery(id+"F0.wireOp",EDGE,"E128");var subQ1=sQuery(id+"F0.wireOp",EDGE,"E57");var subQ3=makeQuery(id+"F0.imprint","INTERSECT",VERTEX,{"derivedFrom":[subQ1,subQ0]});Q87=makeQuery(id+"F0.imprint","IMPRINT",FACE,{"disambiguationData":[TD([[makeQuery(id+"F0.imprint","IMPRINT",EDGE,{"disambiguationData":[TD([[subQ3,1.0]])],"derivedFrom":subQ1}),1.0]])]});}
            var Q88;
            {var subQ0=sQuery(id+"F0.wireOp",EDGE,"E141");var subQ1=sQuery(id+"F0.wireOp",EDGE,"E70");var subQ3=makeQuery(id+"F0.imprint","INTERSECT",VERTEX,{"derivedFrom":[subQ1,subQ0]});Q88=makeQuery(id+"F0.imprint","IMPRINT",FACE,{"disambiguationData":[TD([[makeQuery(id+"F0.imprint","IMPRINT",EDGE,{"disambiguationData":[TD([[subQ3,1.0]])],"derivedFrom":subQ1}),1.0]])]});}
            var Q89;
            {var subQ0=sQuery(id+"F0.wireOp",EDGE,"E104.0");var subQ1=sQuery(id+"F0.wireOp",EDGE,"E103.0");var subQ2=makeQuery(id+"F0.imprint","INTERSECT",VERTEX,{"derivedFrom":[subQ1,subQ0]});Q89=makeQuery(id+"F0.imprint","IMPRINT",FACE,{"disambiguationData":[TD([[makeQuery(id+"F0.imprint","IMPRINT",EDGE,{"disambiguationData":[TD([[subQ2,1.0]])],"derivedFrom":subQ1}),-1.0]])]});}
            var Q90;
            {var subQ0=sQuery(id+"F0.wireOp",EDGE,"E102.0");var subQ1=sQuery(id+"F0.wireOp",EDGE,"E101.0");var subQ2=makeQuery(id+"F0.imprint","INTERSECT",VERTEX,{"derivedFrom":[subQ1,subQ0]});Q90=makeQuery(id+"F0.imprint","IMPRINT",FACE,{"disambiguationData":[TD([[makeQuery(id+"F0.imprint","IMPRINT",EDGE,{"disambiguationData":[TD([[subQ2,1.0]])],"derivedFrom":subQ1}),1.0]])]});}
            var Q91;
            {var subQ4=sQuery(id+"F0.wireOp",EDGE,"E7");var subQ6=sQuery(id+"F0.wireOp",EDGE,"E6.0");var subQ7=makeQuery(id+"F0.imprint","INTERSECT",VERTEX,{"derivedFrom":[subQ6,subQ4]});Q91=makeQuery(id+"F0.imprint","IMPRINT",FACE,{"disambiguationData":[TD([[makeQuery(id+"F0.imprint","IMPRINT",EDGE,{"disambiguationData":[TD([[subQ7,1.0]])],"derivedFrom":subQ6}),-1.0]])]});}
            var Q92;
            {var subQ0=sQuery(id+"F0.wireOp",EDGE,"E104.0");var subQ1=sQuery(id+"F0.wireOp",EDGE,"E103.0");var subQ2=makeQuery(id+"F0.imprint","INTERSECT",VERTEX,{"derivedFrom":[subQ1,subQ0]});Q92=makeQuery(id+"F0.imprint","IMPRINT",FACE,{"disambiguationData":[TD([[makeQuery(id+"F0.imprint","IMPRINT",EDGE,{"disambiguationData":[TD([[subQ2,1.0]])],"derivedFrom":subQ1}),1.0]])]});}
            var Q93;
            {var subQ1=sQuery(id+"F0.wireOp",EDGE,"E29.0");var subQ4=sQuery(id+"F0.wireOp",EDGE,"E43");var subQ5=makeQuery(id+"F0.imprint","INTERSECT",VERTEX,{"derivedFrom":[subQ1,subQ4]});Q93=makeQuery(id+"F0.imprint","IMPRINT",FACE,{"disambiguationData":[TD([[makeQuery(id+"F0.imprint","IMPRINT",EDGE,{"disambiguationData":[TD([[subQ5,1.0]])],"derivedFrom":subQ1}),-1.0]])]});}
            var Q94;
            {var subQ0=sQuery(id+"F0.wireOp",EDGE,"E133");var subQ1=sQuery(id+"F0.wireOp",EDGE,"E97.0");var subQ2=makeQuery(id+"F0.imprint","INTERSECT",VERTEX,{"derivedFrom":[subQ1,subQ0]});Q94=makeQuery(id+"F0.imprint","IMPRINT",FACE,{"disambiguationData":[TD([[makeQuery(id+"F0.imprint","IMPRINT",EDGE,{"disambiguationData":[TD([[subQ2,1.0]])],"derivedFrom":subQ1}),-1.0]])]});}
            var Q95;
            {var subQ0=sQuery(id+"F0.wireOp",EDGE,"E137");var subQ1=sQuery(id+"F0.wireOp",EDGE,"E66");var subQ3=makeQuery(id+"F0.imprint","INTERSECT",VERTEX,{"derivedFrom":[subQ1,subQ0]});Q95=makeQuery(id+"F0.imprint","IMPRINT",FACE,{"disambiguationData":[TD([[makeQuery(id+"F0.imprint","IMPRINT",EDGE,{"disambiguationData":[TD([[subQ3,1.0]])],"derivedFrom":subQ1}),1.0]])]});}
            var Q96;
            {var subQ1=sQuery(id+"F0.wireOp",EDGE,"E30.0");var subQ4=sQuery(id+"F0.wireOp",EDGE,"E44");var subQ5=makeQuery(id+"F0.imprint","INTERSECT",VERTEX,{"derivedFrom":[subQ1,subQ4]});Q96=makeQuery(id+"F0.imprint","IMPRINT",FACE,{"disambiguationData":[TD([[makeQuery(id+"F0.imprint","IMPRINT",EDGE,{"disambiguationData":[TD([[subQ5,1.0]])],"derivedFrom":subQ1}),-1.0]])]});}
            var Q97;
            {var subQ0=sQuery(id+"F0.wireOp",EDGE,"E135");var subQ1=sQuery(id+"F0.wireOp",EDGE,"E99.0");var subQ2=makeQuery(id+"F0.imprint","INTERSECT",VERTEX,{"derivedFrom":[subQ1,subQ0]});Q97=makeQuery(id+"F0.imprint","IMPRINT",FACE,{"disambiguationData":[TD([[makeQuery(id+"F0.imprint","IMPRINT",EDGE,{"disambiguationData":[TD([[subQ2,1.0]])],"derivedFrom":subQ1}),-1.0]])]});}
            var Q98;
            {var subQ0=sQuery(id+"F0.wireOp",EDGE,"E2");var subQ1=sQuery(id+"F0.wireOp",EDGE,"E1");var subQ3=makeQuery(id+"F0.imprint","INTERSECT",VERTEX,{"derivedFrom":[subQ1,subQ0]});Q98=makeQuery(id+"F0.imprint","IMPRINT",FACE,{"disambiguationData":[TD([[makeQuery(id+"F0.imprint","IMPRINT",EDGE,{"disambiguationData":[TD([[subQ3,-1.0]])],"derivedFrom":subQ1}),1.0]])]});}
            var Q99;
            {var subQ0=sQuery(id+"F0.wireOp",EDGE,"E148");var subQ1=sQuery(id+"F0.wireOp",EDGE,"E78");var subQ3=makeQuery(id+"F0.imprint","INTERSECT",VERTEX,{"derivedFrom":[subQ1,subQ0]});Q99=makeQuery(id+"F0.imprint","IMPRINT",FACE,{"disambiguationData":[TD([[makeQuery(id+"F0.imprint","IMPRINT",EDGE,{"disambiguationData":[TD([[subQ3,1.0]])],"derivedFrom":subQ1}),1.0]])]});}
            var Q100;
            {var subQ0=sQuery(id+"F0.wireOp",EDGE,"E47");var subQ1=sQuery(id+"F0.wireOp",EDGE,"E20");var subQ3=makeQuery(id+"F0.imprint","INTERSECT",VERTEX,{"derivedFrom":[subQ1,subQ0]});Q100=makeQuery(id+"F0.imprint","IMPRINT",FACE,{"disambiguationData":[TD([[makeQuery(id+"F0.imprint","IMPRINT",EDGE,{"disambiguationData":[TD([[subQ3,1.0]])],"derivedFrom":subQ1}),1.0]])]});}
            var Q101;
            {var subQ0=sQuery(id+"F0.wireOp",EDGE,"E132");var subQ1=sQuery(id+"F0.wireOp",EDGE,"E96.0");var subQ2=makeQuery(id+"F0.imprint","INTERSECT",VERTEX,{"derivedFrom":[subQ1,subQ0]});Q101=makeQuery(id+"F0.imprint","IMPRINT",FACE,{"disambiguationData":[TD([[makeQuery(id+"F0.imprint","IMPRINT",EDGE,{"disambiguationData":[TD([[subQ2,1.0]])],"derivedFrom":subQ1}),-1.0]])]});}
            var Q102;
            {var subQ1=sQuery(id+"F0.wireOp",EDGE,"E27.0");var subQ4=sQuery(id+"F0.wireOp",EDGE,"E41");var subQ5=makeQuery(id+"F0.imprint","INTERSECT",VERTEX,{"derivedFrom":[subQ1,subQ4]});Q102=makeQuery(id+"F0.imprint","IMPRINT",FACE,{"disambiguationData":[TD([[makeQuery(id+"F0.imprint","IMPRINT",EDGE,{"disambiguationData":[TD([[subQ5,1.0]])],"derivedFrom":subQ1}),-1.0]])]});}
            var Q103;
            {var subQ0=sQuery(id+"F0.wireOp",EDGE,"E36");var subQ1=sQuery(id+"F0.wireOp",EDGE,"E9");var subQ3=makeQuery(id+"F0.imprint","INTERSECT",VERTEX,{"derivedFrom":[subQ1,subQ0]});Q103=makeQuery(id+"F0.imprint","IMPRINT",FACE,{"disambiguationData":[TD([[makeQuery(id+"F0.imprint","IMPRINT",EDGE,{"disambiguationData":[TD([[subQ3,1.0]])],"derivedFrom":subQ1}),1.0]])]});}
            var Q104;
            {var subQ0=sQuery(id+"F0.wireOp",EDGE,"E133");var subQ1=sQuery(id+"F0.wireOp",EDGE,"E62");var subQ3=makeQuery(id+"F0.imprint","INTERSECT",VERTEX,{"derivedFrom":[subQ1,subQ0]});Q104=makeQuery(id+"F0.imprint","IMPRINT",FACE,{"disambiguationData":[TD([[makeQuery(id+"F0.imprint","IMPRINT",EDGE,{"disambiguationData":[TD([[subQ3,1.0]])],"derivedFrom":subQ1}),1.0]])]});}
            var Q105;
            {var subQ0=sQuery(id+"F0.wireOp",EDGE,"E44");var subQ1=sQuery(id+"F0.wireOp",EDGE,"E17");var subQ3=makeQuery(id+"F0.imprint","INTERSECT",VERTEX,{"derivedFrom":[subQ1,subQ0]});Q105=makeQuery(id+"F0.imprint","IMPRINT",FACE,{"disambiguationData":[TD([[makeQuery(id+"F0.imprint","IMPRINT",EDGE,{"disambiguationData":[TD([[subQ3,1.0]])],"derivedFrom":subQ1}),1.0]])]});}
            var Q106;
            {var subQ0=sQuery(id+"F0.wireOp",EDGE,"E134");var subQ1=sQuery(id+"F0.wireOp",EDGE,"E63");var subQ3=makeQuery(id+"F0.imprint","INTERSECT",VERTEX,{"derivedFrom":[subQ1,subQ0]});Q106=makeQuery(id+"F0.imprint","IMPRINT",FACE,{"disambiguationData":[TD([[makeQuery(id+"F0.imprint","IMPRINT",EDGE,{"disambiguationData":[TD([[subQ3,1.0]])],"derivedFrom":subQ1}),1.0]])]});}
            var Q107;
            {var subQ0=sQuery(id+"F0.wireOp",EDGE,"E8");var subQ1=sQuery(id+"F0.wireOp",EDGE,"E7");var subQ3=makeQuery(id+"F0.imprint","INTERSECT",VERTEX,{"derivedFrom":[subQ1,subQ0]});Q107=makeQuery(id+"F0.imprint","IMPRINT",FACE,{"disambiguationData":[TD([[makeQuery(id+"F0.imprint","IMPRINT",EDGE,{"disambiguationData":[TD([[subQ3,1.0]])],"derivedFrom":subQ1}),-1.0]])]});}
            var Q108;
            {var subQ1=sQuery(id+"F0.wireOp",EDGE,"E28.0");var subQ4=sQuery(id+"F0.wireOp",EDGE,"E42");var subQ5=makeQuery(id+"F0.imprint","INTERSECT",VERTEX,{"derivedFrom":[subQ1,subQ4]});Q108=makeQuery(id+"F0.imprint","IMPRINT",FACE,{"disambiguationData":[TD([[makeQuery(id+"F0.imprint","IMPRINT",EDGE,{"disambiguationData":[TD([[subQ5,1.0]])],"derivedFrom":subQ1}),-1.0]])]});}
            var Q109;
            {var subQ0=sQuery(id+"F0.wireOp",EDGE,"E45");var subQ1=sQuery(id+"F0.wireOp",EDGE,"E18");var subQ3=makeQuery(id+"F0.imprint","INTERSECT",VERTEX,{"derivedFrom":[subQ1,subQ0]});Q109=makeQuery(id+"F0.imprint","IMPRINT",FACE,{"disambiguationData":[TD([[makeQuery(id+"F0.imprint","IMPRINT",EDGE,{"disambiguationData":[TD([[subQ3,1.0]])],"derivedFrom":subQ1}),1.0]])]});}
            var Q110;
            {var subQ0=sQuery(id+"F0.wireOp",EDGE,"E135");var subQ1=sQuery(id+"F0.wireOp",EDGE,"E64");var subQ3=makeQuery(id+"F0.imprint","INTERSECT",VERTEX,{"derivedFrom":[subQ1,subQ0]});Q110=makeQuery(id+"F0.imprint","IMPRINT",FACE,{"disambiguationData":[TD([[makeQuery(id+"F0.imprint","IMPRINT",EDGE,{"disambiguationData":[TD([[subQ3,1.0]])],"derivedFrom":subQ1}),1.0]])]});}
            var Q111;
            {var subQ0=sQuery(id+"F0.wireOp",EDGE,"E132");var subQ1=sQuery(id+"F0.wireOp",EDGE,"E61");var subQ3=makeQuery(id+"F0.imprint","INTERSECT",VERTEX,{"derivedFrom":[subQ1,subQ0]});Q111=makeQuery(id+"F0.imprint","IMPRINT",FACE,{"disambiguationData":[TD([[makeQuery(id+"F0.imprint","IMPRINT",EDGE,{"disambiguationData":[TD([[subQ3,1.0]])],"derivedFrom":subQ1}),1.0]])]});}
            var Q112;
            {var subQ0=sQuery(id+"F0.wireOp",EDGE,"E41");var subQ1=sQuery(id+"F0.wireOp",EDGE,"E14");var subQ3=makeQuery(id+"F0.imprint","INTERSECT",VERTEX,{"derivedFrom":[subQ1,subQ0]});Q112=makeQuery(id+"F0.imprint","IMPRINT",FACE,{"disambiguationData":[TD([[makeQuery(id+"F0.imprint","IMPRINT",EDGE,{"disambiguationData":[TD([[subQ3,1.0]])],"derivedFrom":subQ1}),1.0]])]});}
            var Q113;
            {var subQ0=sQuery(id+"F0.wireOp",EDGE,"E136");var subQ1=sQuery(id+"F0.wireOp",EDGE,"E65");var subQ3=makeQuery(id+"F0.imprint","INTERSECT",VERTEX,{"derivedFrom":[subQ1,subQ0]});Q113=makeQuery(id+"F0.imprint","IMPRINT",FACE,{"disambiguationData":[TD([[makeQuery(id+"F0.imprint","IMPRINT",EDGE,{"disambiguationData":[TD([[subQ3,1.0]])],"derivedFrom":subQ1}),1.0]])]});}
            var Q114;
            {var subQ0=sQuery(id+"F0.wireOp",EDGE,"E43");var subQ1=sQuery(id+"F0.wireOp",EDGE,"E16");var subQ3=makeQuery(id+"F0.imprint","INTERSECT",VERTEX,{"derivedFrom":[subQ1,subQ0]});Q114=makeQuery(id+"F0.imprint","IMPRINT",FACE,{"disambiguationData":[TD([[makeQuery(id+"F0.imprint","IMPRINT",EDGE,{"disambiguationData":[TD([[subQ3,1.0]])],"derivedFrom":subQ1}),1.0]])]});}
            var Q115;
            {var subQ0=sQuery(id+"F0.wireOp",EDGE,"E46");var subQ1=sQuery(id+"F0.wireOp",EDGE,"E19");var subQ3=makeQuery(id+"F0.imprint","INTERSECT",VERTEX,{"derivedFrom":[subQ1,subQ0]});Q115=makeQuery(id+"F0.imprint","IMPRINT",FACE,{"disambiguationData":[TD([[makeQuery(id+"F0.imprint","IMPRINT",EDGE,{"disambiguationData":[TD([[subQ3,1.0]])],"derivedFrom":subQ1}),1.0]])]});}
            var Q116;
            {var subQ0=sQuery(id+"F0.wireOp",EDGE,"E42");var subQ1=sQuery(id+"F0.wireOp",EDGE,"E15");var subQ3=makeQuery(id+"F0.imprint","INTERSECT",VERTEX,{"derivedFrom":[subQ1,subQ0]});Q116=makeQuery(id+"F0.imprint","IMPRINT",FACE,{"disambiguationData":[TD([[makeQuery(id+"F0.imprint","IMPRINT",EDGE,{"disambiguationData":[TD([[subQ3,1.0]])],"derivedFrom":subQ1}),1.0]])]});}
            extrude(context, id + "F1", {"entities" : qUnion([Q0, Q1, Q2, Q3, Q4, Q5, Q6, Q7, Q8, Q9, Q10, Q11, Q12, Q13, Q14, Q15, Q16, Q17, Q18, Q19, Q20, Q21, Q22, Q23, Q24, Q25, Q26, Q27, Q28, Q29, Q30, Q31, Q32, Q33, Q34, Q35, Q36, Q37, Q38, Q39, Q40, Q41, Q42, Q43, Q44, Q45, Q46, Q47, Q48, Q49, Q50, Q51, Q52, Q53, Q54, Q55, Q56, Q57, Q58, Q59, Q60, Q61, Q62, Q63, Q64, Q65, Q66, Q67, Q68, Q69, Q70, Q71, Q72, Q73, Q74, Q75, Q76, Q77, Q78, Q79, Q80, Q81, Q82, Q83, Q84, Q85, Q86, Q87, Q88, Q89, Q90, Q91, Q92, Q93, Q94, Q95, Q96, Q97, Q98, Q99, Q100, Q101, Q102, Q103, Q104, Q105, Q106, Q107, Q108, Q109, Q110, Q111, Q112, Q113, Q114, Q115, Q116]), "depth" : 1200 * mm, "offsetDistance" : 25 * mm});
        }
    });
